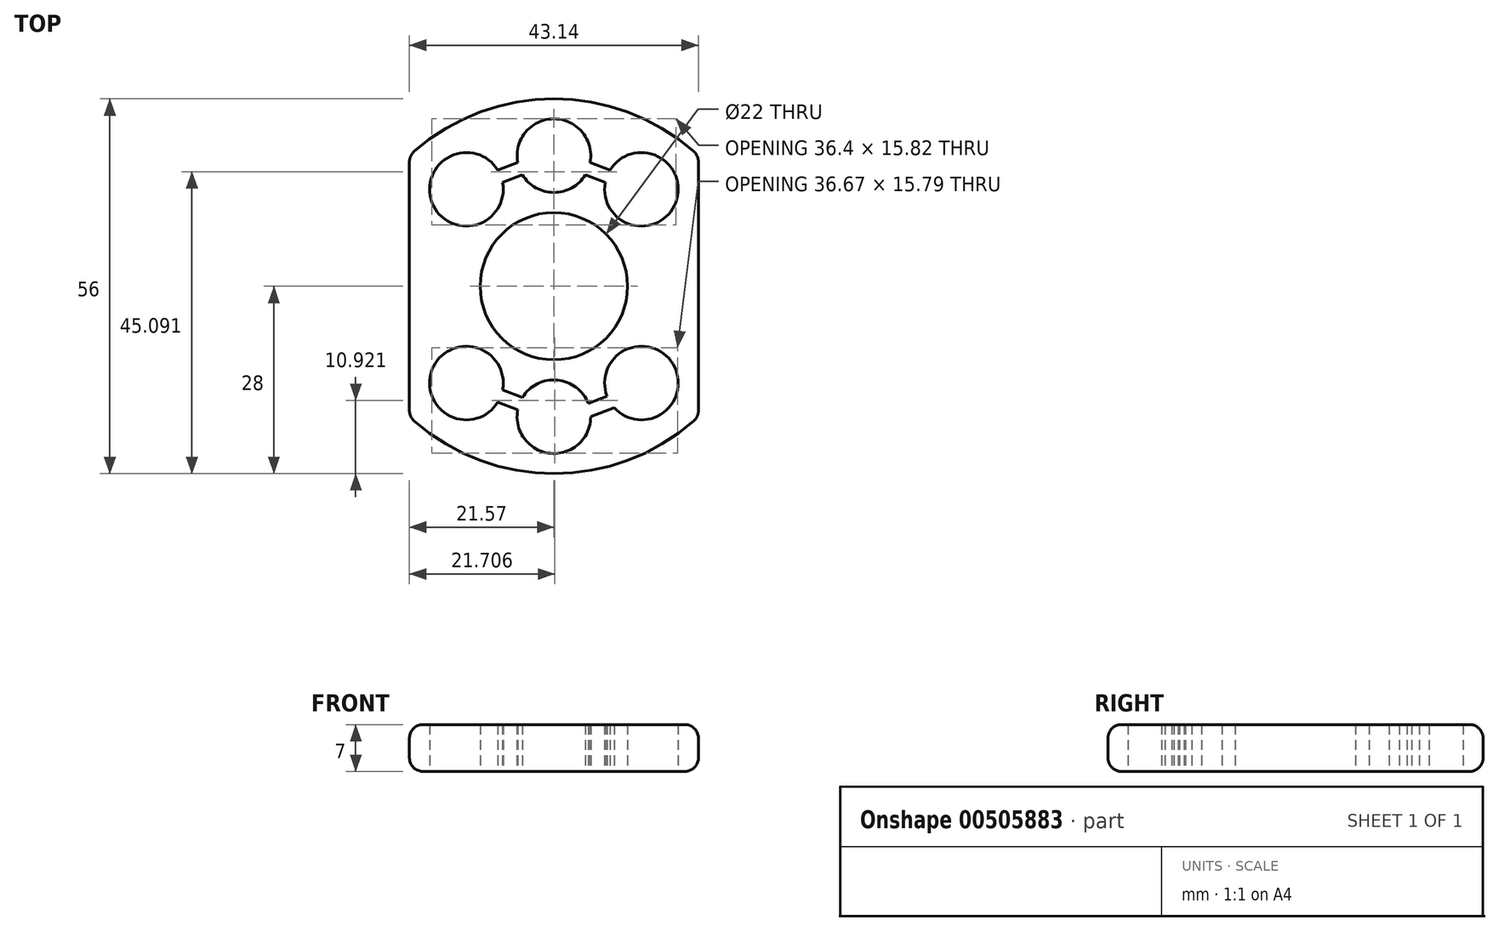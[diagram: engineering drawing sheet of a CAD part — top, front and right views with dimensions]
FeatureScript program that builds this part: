
annotation { "Feature Type Name" : "Feature", "Feature Type Description" : "" }
export const myFeature = defineFeature(function(context is Context, id is Id, definition is map)
    precondition{}
    {
        {
            var Q0;
            Q0=qCreatedBy(makeId("Top.planeOp"),FACE);
            var sketch = newSketch(context, id + "F0", { "sketchPlane" : qUnion([Q0])});
            skCircle(sketch, "E0", {"center": v(-13.07, -14.47) * mm, "radius": 5.5 * mm});
            skCircle(sketch, "E1", {"center": v(13.07, 14.47) * mm, "radius": 5.5 * mm});
            skCircle(sketch, "E2", {"center": v(-13.07, 14.47) * mm, "radius": 5.5 * mm});
            skCircle(sketch, "E3", {"center": v(0, 19.5) * mm, "radius": 5.5 * mm});
            skCircle(sketch, "E4", {"center": v(0, -19.5) * mm, "radius": 5.5 * mm});
            skCircle(sketch, "E5", {"center": v(13.07, -14.47) * mm, "radius": 5.5 * mm});
            skCircle(sketch, "E6", {"center": v(0, 0) * mm, "radius": 11 * mm});
            skLineSegment(sketch, "E7", {"start": v(-7.66, 15.48) * mm, "end": v(-4.69, 16.63) * mm});
            skLineSegment(sketch, "E8", {"start": v(4.69, 16.63) * mm, "end": v(7.66, 15.48) * mm});
            skLineSegment(sketch, "E9", {"start": v(5.4, 18.5) * mm, "end": v(8.38, 17.35) * mm});
            skLineSegment(sketch, "E10", {"start": v(-8.38, 17.35) * mm, "end": v(-5.4, 18.5) * mm});
            skLineSegment(sketch, "E11", {"start": v(5.13, -17.53) * mm, "end": v(7.93, -16.45) * mm});
            skLineSegment(sketch, "E12", {"start": v(-8.38, -17.35) * mm, "end": v(-5.4, -18.5) * mm});
            skLineSegment(sketch, "E13", {"start": v(-7.66, -15.48) * mm, "end": v(-4.69, -16.63) * mm});
            skLineSegment(sketch, "E14", {"start": v(5.5, -19.5) * mm, "end": v(9, -18.18) * mm});
            skLineSegment(sketch, "E15", {"start": v(-21.57, 19.5) * mm, "end": v(-21.57, -19.5) * mm});
            skLineSegment(sketch, "E16", {"start": v(21.57, 19.5) * mm, "end": v(21.57, -19.5) * mm});
            skArc(sketch, "E17", {"start": v(21.57, 19.5) * mm, "mid": v(0, 28) * mm, "end": v(-21.57, 19.5) * mm});
            skArc(sketch, "E18", {"start": v(-21.57, -19.5) * mm, "mid": v(0, -28) * mm, "end": v(21.57, -19.5) * mm});
            skSolve(sketch);
        }
        {
            var Q0;
            Q0 = qSketchRegion(id + "F0", true);
            extrude(context, id + "F1", {"entities" : qUnion([Q0]), "depth" : 7 * mm});
        }
        {
            var Q0;
            Q0=makeQuery(id+"F1.opExtrude","SWEPT_FACE",FACE,{"disambiguationData":[OSD([sQuery(id+"F0.wireOp",EDGE,"E17")])]});
            var Q1;
            Q1=makeQuery(id+"F1.opExtrude","SWEPT_FACE",FACE,{"disambiguationData":[OSD([sQuery(id+"F0.wireOp",EDGE,"E15")])]});
            var Q2;
            Q2=makeQuery(id+"F1.opExtrude","SWEPT_FACE",FACE,{"disambiguationData":[OSD([sQuery(id+"F0.wireOp",EDGE,"E18")])]});
            var Q3;
            Q3=makeQuery(id+"F1.opExtrude","SWEPT_FACE",FACE,{"disambiguationData":[OSD([sQuery(id+"F0.wireOp",EDGE,"E16")])]});
            fillet(context, id + "F2", {"entities" : qUnion([Q0, Q1, Q2, Q3]), "radius" : 2 * mm, "tangentPropagation" : true, "allowEdgeOverflow" : false});
        }
    });
